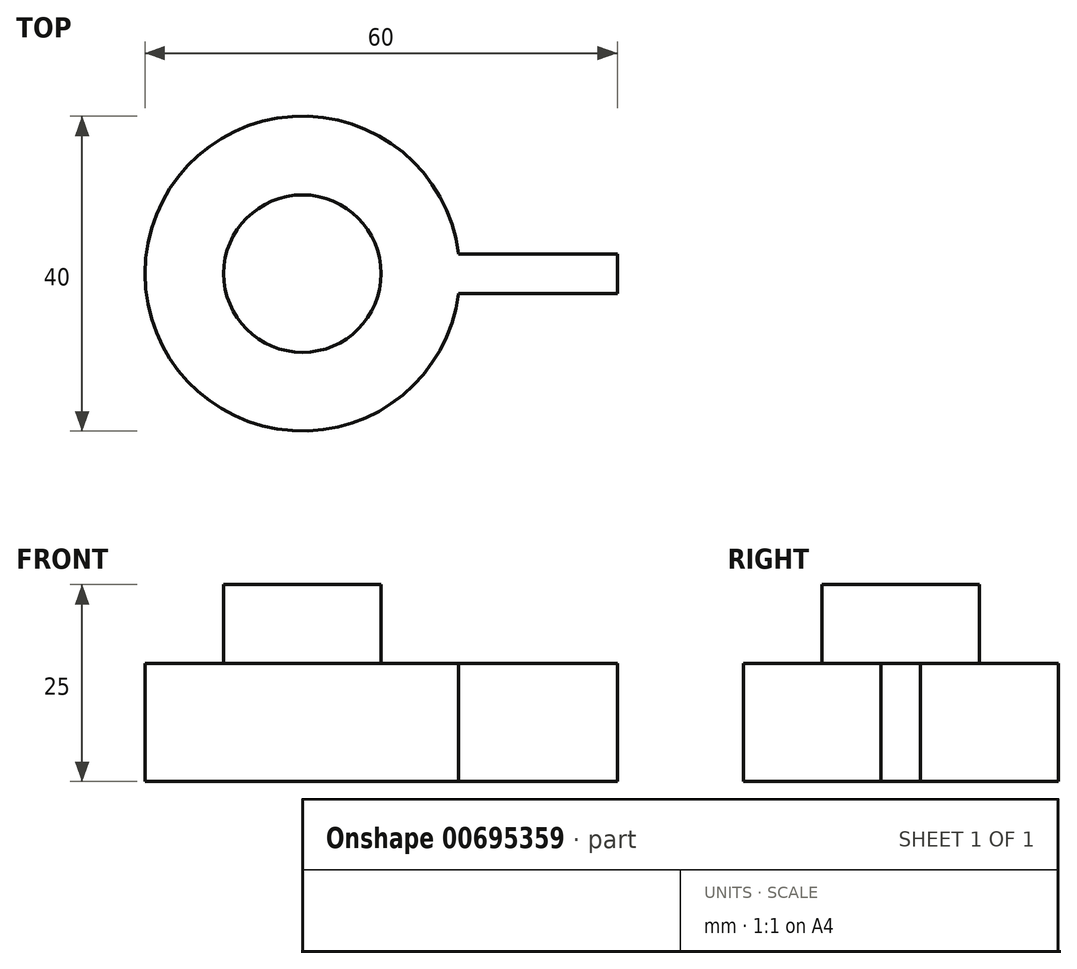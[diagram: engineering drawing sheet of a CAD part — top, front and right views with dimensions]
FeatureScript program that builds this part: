
annotation { "Feature Type Name" : "Feature", "Feature Type Description" : "" }
export const myFeature = defineFeature(function(context is Context, id is Id, definition is map)
    precondition{}
    {
        {
            var Q0;
            Q0=qCreatedBy(makeId("Top.planeOp"),FACE);
            var sketch = newSketch(context, id + "F0", { "sketchPlane" : qUnion([Q0])});
            skCircle(sketch, "E0", {"center": v(0, 0) * mm, "radius": 20 * mm});
            skSolve(sketch);
        }
        {
            var Q0;
            Q0 = qSketchRegion(id + "F0", true);
            extrude(context, id + "F1", {"entities" : qUnion([Q0]), "depth" : 15 * mm, "offsetDistance" : 25 * mm});
        }
        {
            var Q0;
            Q0=qCreatedBy(makeId("Top.planeOp"),FACE);
            var sketch = newSketch(context, id + "F2", { "sketchPlane" : qUnion([Q0])});
            skLineSegment(sketch, "E1.bottom", {"start": v(0, 0) * mm, "end": v(40, 0) * mm});
            skLineSegment(sketch, "E1.top", {"start": v(0, 2.5) * mm, "end": v(40, 2.5) * mm});
            skLineSegment(sketch, "E1.left", {"start": v(0, 0) * mm, "end": v(0, 2.5) * mm});
            skLineSegment(sketch, "E1.right", {"start": v(40, 0) * mm, "end": v(40, 2.5) * mm});
            skLineSegment(sketch, "E2.top", {"start": v(0, -2.5) * mm, "end": v(40, -2.5) * mm});
            skLineSegment(sketch, "E2.left", {"start": v(0, 0) * mm, "end": v(0, -2.5) * mm});
            skLineSegment(sketch, "E2.right", {"start": v(40, 0) * mm, "end": v(40, -2.5) * mm});
            skSolve(sketch);
        }
        {
            var Q0;
            Q0 = qSketchRegion(id + "F2", true);
            extrude(context, id + "F3", {"entities" : qUnion([Q0]), "operationType" : NewBodyOperationType.ADD, "depth" : 15 * mm, "offsetDistance" : 25 * mm});
        }
        {
            var Q0;
            Q0=qCreatedBy(makeId("Top.planeOp"),FACE);
            var sketch = newSketch(context, id + "F4", { "sketchPlane" : qUnion([Q0])});
            skCircle(sketch, "E3", {"center": v(0, 0) * mm, "radius": 10 * mm});
            skSolve(sketch);
        }
        {
            var Q0;
            Q0 = qSketchRegion(id + "F4", true);
            extrude(context, id + "F5", {"entities" : qUnion([Q0]), "operationType" : NewBodyOperationType.ADD, "depth" : 25 * mm, "offsetDistance" : 25 * mm});
        }
    });
